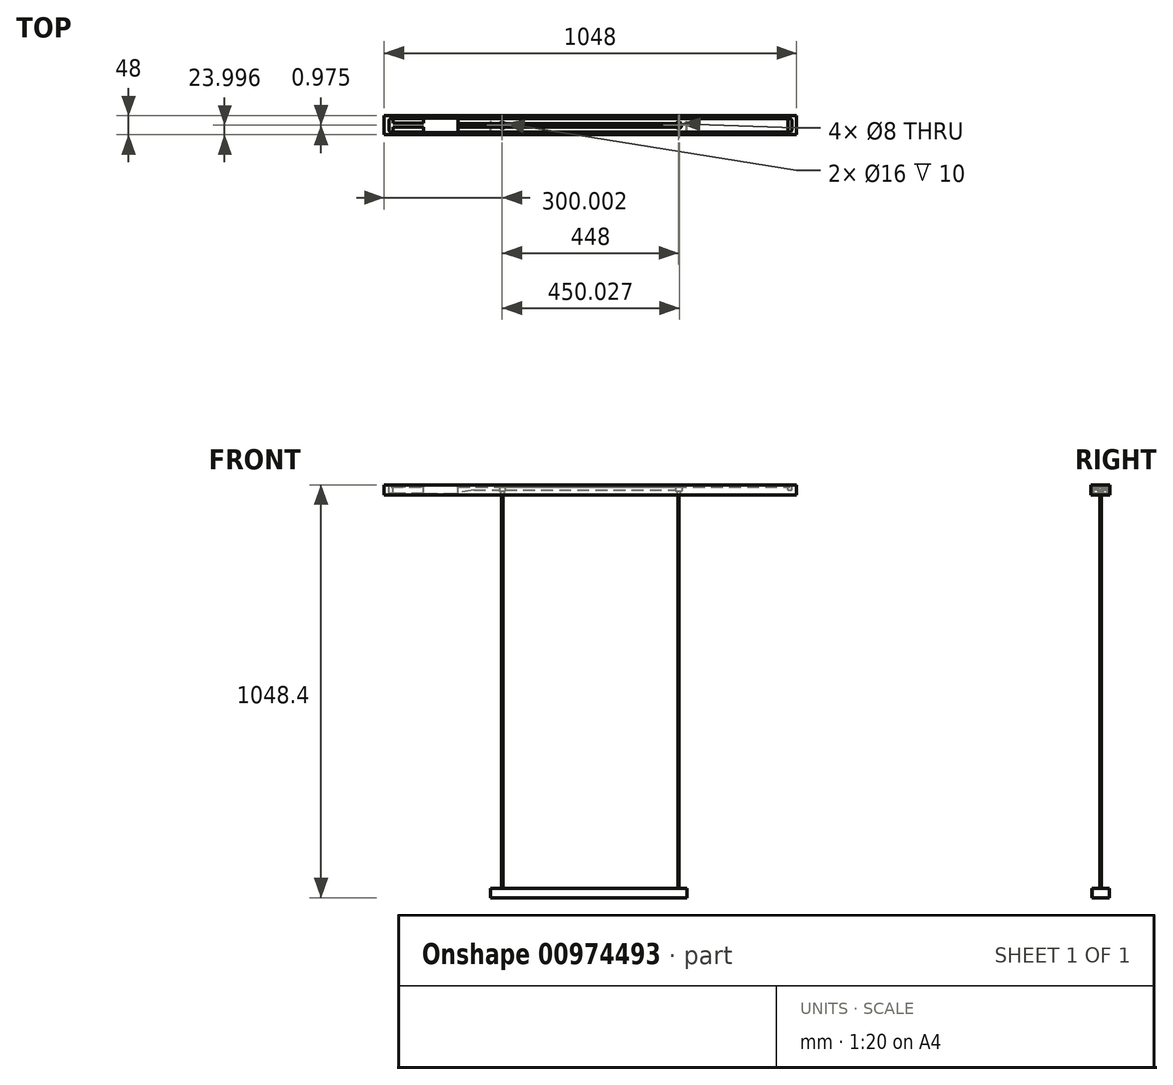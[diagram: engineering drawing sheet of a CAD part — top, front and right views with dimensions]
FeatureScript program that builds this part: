
annotation { "Feature Type Name" : "Feature", "Feature Type Description" : "" }
export const myFeature = defineFeature(function(context is Context, id is Id, definition is map)
    precondition{}
    {
        {
            var Q0;
            Q0=qCreatedBy(makeId("Top.planeOp"),FACE);
            var sketch = newSketch(context, id + "F0", { "sketchPlane" : qUnion([Q0])});
            skLineSegment(sketch, "E0.bottom", {"start": v(-504.26, 24.36) * mm, "end": v(543.74, 24.36) * mm});
            skLineSegment(sketch, "E0.top", {"start": v(-504.26, -23.64) * mm, "end": v(543.74, -23.64) * mm});
            skLineSegment(sketch, "E0.left", {"start": v(-504.26, 24.36) * mm, "end": v(-504.26, -23.64) * mm});
            skLineSegment(sketch, "E0.right", {"start": v(543.74, 24.36) * mm, "end": v(543.74, -23.64) * mm});
            skSolve(sketch);
        }
        {
            var Q0;
            Q0=makeQuery(id+"F0.imprint","IMPRINT",FACE,{"disambiguationData":[TD([[makeQuery(id+"F0.imprint","IMPRINT",EDGE,{"derivedFrom":sQuery(id+"F0.wireOp",EDGE,"E0.bottom")}),-1.0]])]});
            extrude(context, id + "F1", {"entities" : qUnion([Q0]), "depth" : 25 * mm, "offsetDistance" : 25 * mm});
        }
        {
            var Q0;
            Q0=makeQuery(id+"F1.opExtrude","CAP_FACE",FACE,{"disambiguationData":[OSD([sQuery(id+"F0.wireOp",EDGE,"E0.bottom"),sQuery(id+"F0.wireOp",EDGE,"E0.top"),sQuery(id+"F0.wireOp",EDGE,"E0.left"),sQuery(id+"F0.wireOp",EDGE,"E0.right")])],"isStart":false});
            var sketch = newSketch(context, id + "F2", { "sketchPlane" : qUnion([Q0])});
            skLineSegment(sketch, "E1.bottom", {"start": v(-486.76, 17.36) * mm, "end": v(526.24, 17.36) * mm});
            skLineSegment(sketch, "E1.top", {"start": v(-486.76, -16.64) * mm, "end": v(526.24, -16.64) * mm});
            skLineSegment(sketch, "E1.left", {"start": v(-491.76, 12.36) * mm, "end": v(-491.76, -11.64) * mm});
            skLineSegment(sketch, "E1.right", {"start": v(531.24, 12.36) * mm, "end": v(531.24, -11.64) * mm});
            skPoint(sketch, "E2.visualSharp", {"position": v(-491.76, 17.36) * mm});
            skArc(sketch, "E2.filletArc", {"start": v(-486.76, 17.36) * mm, "mid": v(-490.3, 15.9) * mm, "end": v(-491.76, 12.36) * mm});
            skPoint(sketch, "E3.visualSharp", {"position": v(-491.76, -16.64) * mm});
            skArc(sketch, "E3.filletArc", {"start": v(-491.76, -11.64) * mm, "mid": v(-490.3, -15.18) * mm, "end": v(-486.76, -16.64) * mm});
            skPoint(sketch, "E4.visualSharp", {"position": v(531.24, -16.64) * mm});
            skArc(sketch, "E4.filletArc", {"start": v(526.24, -16.64) * mm, "mid": v(529.78, -15.18) * mm, "end": v(531.24, -11.64) * mm});
            skPoint(sketch, "E5.visualSharp", {"position": v(531.24, 17.36) * mm});
            skArc(sketch, "E5.filletArc", {"start": v(531.24, 12.36) * mm, "mid": v(529.78, 15.9) * mm, "end": v(526.24, 17.36) * mm});
            skLineSegment(sketch, "E6", {"start": v(-491.76, 17.36) * mm, "end": v(-486.76, 17.36) * mm});
            skSolve(sketch);
        }
        {
            var Q0;
            Q0=makeQuery(id+"F2.imprint","IMPRINT",FACE,{"disambiguationData":[TD([[makeQuery(id+"F2.imprint","IMPRINT",EDGE,{"derivedFrom":sQuery(id+"F2.wireOp",EDGE,"E1.bottom")}),-1.0]])]});
            extrude(context, id + "F3", {"entities" : qUnion([Q0]), "operationType" : NewBodyOperationType.REMOVE, "depth" : -5 * mm, "offsetDistance" : 25 * mm});
        }
        {
            var Q0;
            Q0=makeQuery(id+"F1.opExtrude","CAP_FACE",FACE,{"disambiguationData":[OSD([sQuery(id+"F0.wireOp",EDGE,"E0.bottom"),sQuery(id+"F0.wireOp",EDGE,"E0.top"),sQuery(id+"F0.wireOp",EDGE,"E0.left"),sQuery(id+"F0.wireOp",EDGE,"E0.right")])],"isStart":false});
            var sketch = newSketch(context, id + "F4", { "sketchPlane" : qUnion([Q0])});
            skLineSegment(sketch, "E7.bottom", {"start": v(-399.26, 18.86) * mm, "end": v(-321.26, 18.86) * mm});
            skLineSegment(sketch, "E7.top", {"start": v(-399.26, -18.14) * mm, "end": v(-321.26, -18.14) * mm});
            skLineSegment(sketch, "E7.left", {"start": v(-404.26, 13.86) * mm, "end": v(-404.26, -13.14) * mm});
            skLineSegment(sketch, "E7.right", {"start": v(-316.26, 13.86) * mm, "end": v(-316.26, -13.14) * mm});
            skPoint(sketch, "E8.visualSharp", {"position": v(-404.26, 18.86) * mm});
            skArc(sketch, "E8.filletArc", {"start": v(-399.26, 18.86) * mm, "mid": v(-402.8, 17.4) * mm, "end": v(-404.26, 13.86) * mm});
            skPoint(sketch, "E9.visualSharp", {"position": v(-316.26, 18.86) * mm});
            skArc(sketch, "E9.filletArc", {"start": v(-316.26, 13.86) * mm, "mid": v(-317.72, 17.4) * mm, "end": v(-321.26, 18.86) * mm});
            skPoint(sketch, "E10.visualSharp", {"position": v(-404.26, -18.14) * mm});
            skArc(sketch, "E10.filletArc", {"start": v(-404.26, -13.14) * mm, "mid": v(-402.8, -16.68) * mm, "end": v(-399.26, -18.14) * mm});
            skPoint(sketch, "E11.visualSharp", {"position": v(-316.26, -18.14) * mm});
            skArc(sketch, "E11.filletArc", {"start": v(-321.26, -18.14) * mm, "mid": v(-317.72, -16.68) * mm, "end": v(-316.26, -13.14) * mm});
            skLineSegment(sketch, "E12.bottom", {"start": v(-404.26, 5.36) * mm, "end": v(-481.76, 5.36) * mm});
            skLineSegment(sketch, "E12.top", {"start": v(-404.26, -4.64) * mm, "end": v(-481.76, -4.64) * mm});
            skLineSegment(sketch, "E12.left", {"start": v(-404.26, 5.36) * mm, "end": v(-404.26, -4.64) * mm});
            skLineSegment(sketch, "E12.right", {"start": v(-481.76, 5.36) * mm, "end": v(-481.76, -4.64) * mm});
            skCircle(sketch, "E13", {"center": v(-486.76, 12.36) * mm, "radius": 5 * mm});
            skCircle(sketch, "E14", {"center": v(-486.76, -11.64) * mm, "radius": 5 * mm});
            skLineSegment(sketch, "E15.bottom", {"start": v(-491.76, 12.36) * mm, "end": v(-481.76, 12.36) * mm});
            skLineSegment(sketch, "E15.top", {"start": v(-491.76, -11.64) * mm, "end": v(-481.76, -11.64) * mm});
            skLineSegment(sketch, "E15.left", {"start": v(-491.76, 12.36) * mm, "end": v(-491.76, -11.64) * mm});
            skLineSegment(sketch, "E15.right", {"start": v(-481.76, 12.36) * mm, "end": v(-481.76, -11.64) * mm});
            skPoint(sketch, "E16", {"position": v(-204.26, 0.36) * mm});
            skPoint(sketch, "E17", {"position": v(243.74, 0.36) * mm});
            skSolve(sketch);
        }
        {
            var Q0;
            Q0 = qSketchRegion(id + "F4", true);
            extrude(context, id + "F5", {"entities" : qUnion([Q0]), "operationType" : NewBodyOperationType.REMOVE, "oppositeDirection" : true, "depth" : 21 * mm, "offsetDistance" : 25 * mm});
        }
        {
            var Q0;
            Q0=sQuery(id+"F4.wireOp",VERTEX,"E16");
            var Q1;
            Q1=sQuery(id+"F4.wireOp",VERTEX,"E17");
            var Q2;
            Q2=makeQuery(id+"F1.opExtrude","SWEPT_BODY",BODY,{"disambiguationData":[OSD([sQuery(id+"F0.wireOp",EDGE,"E0.bottom"),sQuery(id+"F0.wireOp",EDGE,"E0.top"),sQuery(id+"F0.wireOp",EDGE,"E0.left"),sQuery(id+"F0.wireOp",EDGE,"E0.right")])]});
            hole(context, id + "F6", {"style" : HoleStyle.C_BORE, "endStyle" : HoleEndStyle.THROUGH, "holeDiameter" : 8 * mm, "cBoreDiameter" : 16 * mm, "cBoreDepth" : 15 * mm, "majorDiameter" : 5 * mm, "isTappedThrough" : true, "tappedDepth" : 12 * mm, "tapClearance" : 3, "locations" : qUnion([Q0, Q1]), "scope" : qUnion([Q2]), "startStyle" : HoleStartStyle.SKETCH});
        }
        {
            var Q0;
            {var subQ0=sQuery(id+"F2.wireOp",EDGE,"E1.right");var subQ1=sQuery(id+"F2.wireOp",EDGE,"E4.filletArc");var subQ2=sQuery(id+"F2.wireOp",EDGE,"E1.top");var subQ3=sQuery(id+"F2.wireOp",EDGE,"E1.bottom");var subQ4=sQuery(id+"F2.wireOp",EDGE,"E5.filletArc");Q0=makeQuery(id+"F5.boolean.opBoolean","SPLIT",FACE,{"disambiguationData":[TD([makeQuery(id+"F3.boolean.opBoolean","COPY",FACE,{"derivedFrom":makeQuery(id+"F3.opExtrude","SWEPT_FACE",FACE,{"disambiguationData":[OSD([subQ0])]})})])],"derivedFrom":makeQuery(id+"F3.boolean.opBoolean","COPY",FACE,{"derivedFrom":makeQuery(id+"F3.opExtrude","CAP_FACE",FACE,{"disambiguationData":[OSD([subQ3,subQ2,sQuery(id+"F2.wireOp",EDGE,"E1.left"),subQ0,sQuery(id+"F2.wireOp",EDGE,"E2.filletArc"),sQuery(id+"F2.wireOp",EDGE,"E3.filletArc"),subQ1,subQ4])],"isStart":false})})});}
            var sketch = newSketch(context, id + "F7", { "sketchPlane" : qUnion([Q0])});
            skLineSegment(sketch, "E18.bottom", {"start": v(-316.41, 4.36) * mm, "end": v(236.81, 4.36) * mm});
            skLineSegment(sketch, "E18.top", {"start": v(-316.41, -3.64) * mm, "end": v(236.81, -3.64) * mm});
            skLineSegment(sketch, "E18.left", {"start": v(-316.41, 4.36) * mm, "end": v(-316.41, -3.64) * mm});
            skLineSegment(sketch, "E18.right", {"start": v(236.81, 4.36) * mm, "end": v(236.81, -3.64) * mm});
            skCircle(sketch, "E19", {"center": v(526.24, 12.36) * mm, "radius": 5 * mm});
            skCircle(sketch, "E20", {"center": v(526.24, -11.64) * mm, "radius": 5 * mm});
            skLineSegment(sketch, "E21.bottom", {"start": v(531.24, 12.36) * mm, "end": v(521.24, 12.36) * mm});
            skLineSegment(sketch, "E21.top", {"start": v(531.24, -11.6) * mm, "end": v(521.24, -11.6) * mm});
            skLineSegment(sketch, "E21.left", {"start": v(531.24, 12.36) * mm, "end": v(531.24, -11.6) * mm});
            skLineSegment(sketch, "E21.right", {"start": v(521.24, 12.36) * mm, "end": v(521.24, -11.6) * mm});
            skSolve(sketch);
        }
        {
            var Q0;
            Q0 = qSketchRegion(id + "F7", true);
            extrude(context, id + "F8", {"entities" : qUnion([Q0]), "operationType" : NewBodyOperationType.REMOVE, "oppositeDirection" : true, "depth" : 8 * mm, "offsetDistance" : 25 * mm});
        }
        {
            var Q0;
            Q0=makeQuery(id+"F8.boolean.opBoolean","INTERSECT",EDGE,{"derivedFrom":[makeQuery(id+"F5.boolean.opBoolean","COPY",FACE,{"derivedFrom":makeQuery(id+"F5.opExtrude","SWEPT_FACE",FACE,{"disambiguationData":[OSD([sQuery(id+"F4.wireOp",EDGE,"E7.right")])]})}),makeQuery(id+"F8.opExtrude","CAP_FACE",FACE,{"disambiguationData":[OSD([sQuery(id+"F7.wireOp",EDGE,"E18.bottom"),sQuery(id+"F7.wireOp",EDGE,"E18.top"),sQuery(id+"F7.wireOp",EDGE,"E18.left"),sQuery(id+"F7.wireOp",EDGE,"E18.right")])],"isStart":false})]});
            chamfer(context, id + "F9", {"entities" : qUnion([Q0]), "chamferType" : ChamferType.TWO_OFFSETS, "width1" : 6 * mm, "oppositeDirection" : false, "width2" : 40 * mm, "tangentPropagation" : true});
        }
        {
            var Q0;
            Q0=makeQuery(id+"F1.opExtrude","CAP_FACE",FACE,{"disambiguationData":[OSD([sQuery(id+"F0.wireOp",EDGE,"E0.bottom"),sQuery(id+"F0.wireOp",EDGE,"E0.top"),sQuery(id+"F0.wireOp",EDGE,"E0.left"),sQuery(id+"F0.wireOp",EDGE,"E0.right")])],"isStart":true});
            var sketch = newSketch(context, id + "F10", { "sketchPlane" : qUnion([Q0])});
            skCircle(sketch, "E22", {"center": v(-204.26, -0.36) * mm, "radius": 1.5 * mm});
            skCircle(sketch, "E23", {"center": v(243.74, -0.36) * mm, "radius": 1.5 * mm});
            skSolve(sketch);
        }
        {
            var Q0;
            Q0 = qSketchRegion(id + "F10", true);
            extrude(context, id + "F11", {"entities" : qUnion([Q0]), "depth" : 1000 * mm, "offsetDistance" : 25 * mm});
        }
        {
            var Q0;
            Q0=makeQuery(id+"F11.opExtrude","CAP_FACE",FACE,{"disambiguationData":[OSD([sQuery(id+"F10.wireOp",EDGE,"E22")])],"isStart":false});
            var sketch = newSketch(context, id + "F12", { "sketchPlane" : qUnion([Q0])});
            skLineSegment(sketch, "E24.bottom", {"start": v(-234.26, 21.31) * mm, "end": v(265.74, 21.31) * mm});
            skLineSegment(sketch, "E24.top", {"start": v(-234.26, -22.69) * mm, "end": v(265.74, -22.69) * mm});
            skLineSegment(sketch, "E24.left", {"start": v(-234.26, 21.31) * mm, "end": v(-234.26, -22.69) * mm});
            skLineSegment(sketch, "E24.right", {"start": v(265.74, 21.31) * mm, "end": v(265.74, -22.69) * mm});
            skPoint(sketch, "E25", {"position": v(-204.26, -0.36) * mm});
            skPoint(sketch, "E26", {"position": v(245.77, -1.33) * mm});
            skSolve(sketch);
        }
        {
            var Q0;
            Q0 = qSketchRegion(id + "F12", true);
            extrude(context, id + "F13", {"entities" : qUnion([Q0]), "depth" : 23.4 * mm, "offsetDistance" : 25 * mm});
        }
        {
            var Q0;
            Q0=makeQuery(id+"F13.opExtrude","CAP_FACE",FACE,{"disambiguationData":[OSD([sQuery(id+"F12.wireOp",EDGE,"E24.bottom"),sQuery(id+"F12.wireOp",EDGE,"E24.top"),sQuery(id+"F12.wireOp",EDGE,"E24.left"),sQuery(id+"F12.wireOp",EDGE,"E24.right")])],"isStart":false});
            var sketch = newSketch(context, id + "F14", { "sketchPlane" : qUnion([Q0])});
            skLineSegment(sketch, "E27.bottom", {"start": v(-232.26, 19.31) * mm, "end": v(263.74, 19.31) * mm});
            skLineSegment(sketch, "E27.top", {"start": v(-232.26, -20.69) * mm, "end": v(263.74, -20.69) * mm});
            skLineSegment(sketch, "E27.left", {"start": v(-232.26, 19.31) * mm, "end": v(-232.26, -20.69) * mm});
            skLineSegment(sketch, "E27.right", {"start": v(263.74, 19.31) * mm, "end": v(263.74, -20.69) * mm});
            skSolve(sketch);
        }
        {
            var Q0;
            Q0=makeQuery(id+"F14.imprint","IMPRINT",FACE,{"disambiguationData":[TD([[makeQuery(id+"F14.imprint","IMPRINT",EDGE,{"derivedFrom":sQuery(id+"F14.wireOp",EDGE,"E27.bottom")}),-1.0]])]});
            extrude(context, id + "F15", {"entities" : qUnion([Q0]), "operationType" : NewBodyOperationType.REMOVE, "oppositeDirection" : true, "depth" : 22.5 * mm, "offsetDistance" : 25 * mm});
        }
        {
            var Q0;
            Q0=sQuery(id+"F12.wireOp",VERTEX,"E25");
            var Q1;
            Q1=makeQuery(id+"F13.opExtrude","SWEPT_BODY",BODY,{"disambiguationData":[OSD([sQuery(id+"F12.wireOp",EDGE,"E24.bottom"),sQuery(id+"F12.wireOp",EDGE,"E24.top"),sQuery(id+"F12.wireOp",EDGE,"E24.left"),sQuery(id+"F12.wireOp",EDGE,"E24.right")])]});
            hole(context, id + "F16", {"style" : HoleStyle.SIMPLE, "endStyle" : HoleEndStyle.THROUGH, "oppositeDirection" : true, "holeDiameter" : 8 * mm, "majorDiameter" : 5 * mm, "isTappedThrough" : true, "tappedDepth" : 12 * mm, "tapClearance" : 3, "locations" : qUnion([Q0]), "scope" : qUnion([Q1]), "startStyle" : HoleStartStyle.SKETCH});
        }
        {
            var Q0;
            Q0=sQuery(id+"F12.wireOp",VERTEX,"E26");
            var Q1;
            Q1=makeQuery(id+"F13.opExtrude","SWEPT_BODY",BODY,{"disambiguationData":[OSD([sQuery(id+"F12.wireOp",EDGE,"E24.bottom"),sQuery(id+"F12.wireOp",EDGE,"E24.top"),sQuery(id+"F12.wireOp",EDGE,"E24.left"),sQuery(id+"F12.wireOp",EDGE,"E24.right")])]});
            hole(context, id + "F17", {"style" : HoleStyle.SIMPLE, "endStyle" : HoleEndStyle.THROUGH, "oppositeDirection" : true, "holeDiameter" : 8 * mm, "majorDiameter" : 5 * mm, "isTappedThrough" : true, "tappedDepth" : 12 * mm, "tapClearance" : 3, "locations" : qUnion([Q0]), "scope" : qUnion([Q1]), "startStyle" : HoleStartStyle.SKETCH});
        }
    });
